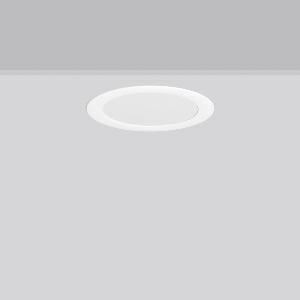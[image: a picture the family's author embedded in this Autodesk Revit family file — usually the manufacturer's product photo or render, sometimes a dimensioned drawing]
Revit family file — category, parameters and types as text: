
# Revit family: toledo_flat_round_e_672224_002_1_a579
name_source: partatom
category: Lighting Fixtures
units: mm (PartAtom-declared; Revit-internal decimal feet)

## family parameters
Cut with Voids When Loaded = No
Host = Face
Light Source = No
Part Type = Normal
Room Calculation Point = No
Round Connector Dimension = Use Diameter
Shared = No

## types (1)
- TOLEDO FLAT round E (1 x LED Modul 840, 1800 lm, 4000)
    Apparent Load = 17 VA
    CIE Flux Codes = 48 79 96 100 100
    Color Rendering = 80
    Color Temperature = 4000
    Default Elevation = 1800 mm  [stored 5.90551 ft]
    Description = Series: TOLEDO FLAT round
Ultra thin recessed downlight. For escape route illumination. Housing: die-cast aluminium, powder-coated. Lightguide and diffuser made of non-yellowing plastic (PMMA). Diffuser opal matt plastic. Ceiling installation with spring system. Including separate LED converter with connecting cable 250 mm. Self-contained system with automatic self-test. External driver with simple plug-in locking system. 
Colour: white
Diameter: 255 mm
Height: 3 mm
Cut-out diameter: 234 mm
Recess height: 100 mm
Luminaire: recess height: 60-80 mm
Weight: 1.76 kg
Operating mode: maintained power mode
Duration time: 3 h
Lamp: LED
Socket: without socket
Colour temperature: 4000K
Colour rendering index (CRI): 80
System power: 17 W
Rated luminous flux: 1800 lm
Luminous flux, emergency: 460 lm
System power, emergency: -
Control gear: Regulated power supply
Protection class: I
Type of protection: IP 54
    Height = 0 mm  [stored 0 ft]
    Lamp = 1 x LED Modul 840
    Lamp Light Flux = 1800 lm
    Lamp count = 1
    Length = 255 mm
    Lifetime = 50000 h
    Luminous efficacy = 106 lm/W
    Manufacturer = RZB
    ModVariant = No
    Model = 672224.002.1
    Mounting Place = Ceiling
    Mounting Type = Recessed
    Number of Poles = 1
    OnlyDefault = Yes
    Power Factor = 1
    Product Name = TOLEDO FLAT round E
    Product group = Recessed downlights
    ProductGroupID = 402
    Protection Class = Protection class I
    Protection Degree = IP 40
    RLX_Detail_Level = 1
    RLX_Emergency_Light_Flux = 460 lm
    RLX_Emergency_Type = 3
    RLX_Emergency_Type_DB = Yes
    RlxData = <blob elided: 30449 chars, md5=35fe5619>
    Socket = socket
    Standby Power = 0 W
    System Light Flux = 1800 lm
    System Power = 17 W
    Type Comments = Product without accessories
    Type Image = 901453.002.jpg
    URL = http://relux.com
    VarID = ---
    Voltage = 0 V
    Weight = 0.00 kg
    Width = 0 mm  [stored 0 ft]

note: [stored X ft] marks values corroborated as IEEE doubles in the binary element streams (Revit-internal decimal feet)

## geometry (parser evidence)
native form markers: Blend x4, Sweep x11
no freeform markers — native parametric forms only
